FCSTD DOCUMENT  (FreeCAD 0.16R)
Label: PumpHolder
License: All rights reserved
LicenseURL: http://en.wikipedia.org/wiki/All_rights_reserved
objects: Sketcher::SketchObject×9, PartDesign::Pocket×5, PartDesign::Pad×3, PartDesign::Fillet×2, PartDesign::Chamfer×1, Mesh::Feature×1
note: 28 computed .brp shape members not serialized (recipe doc carries the construction recipe); baked Part::Feature solids carry a one-line shape summary decoded from their .brp

FEATURE [Sketcher::SketchObject] Sketch
  sketch-geometry (4):
    g0: LineSegment StartX=-10 StartY=52.5 StartZ=0 EndX=10 EndY=52.5 EndZ=0
    g1: LineSegment StartX=10 StartY=52.5 StartZ=0 EndX=10 EndY=-52.5 EndZ=0
    g2: LineSegment StartX=10 StartY=-52.5 StartZ=0 EndX=-10 EndY=-52.5 EndZ=0
    g3: LineSegment StartX=-10 StartY=-52.5 StartZ=0 EndX=-10 EndY=52.5 EndZ=0
  constraints (11):
    c: Coincident(g0,g1)
    c: Coincident(g1,g2)
    c: Coincident(g2,g3)
    c: Coincident(g3,g0)
    c: Horizontal(g0)
    c: Horizontal(g2)
    c: Vertical(g1)
    c: Vertical(g3)
    c: Symmetric(g0,g2,g-1)
    c: Distance(g1) = 105
    c: Distance(g2) = 20
FEATURE [PartDesign::Pad] Pad
  Length = 5
  Length2 = 100
  Sketch = -> Sketch
  Type = 0
FEATURE [Sketcher::SketchObject] Sketch004
  Placement = pos=(0,0,5) rot=(0,0,1;0rad)
  sketch-geometry (4):
    g0: LineSegment StartX=-7 StartY=52.5 StartZ=0 EndX=7 EndY=52.5 EndZ=0
    g1: LineSegment StartX=7 StartY=52.5 StartZ=0 EndX=7 EndY=-52.5 EndZ=0
    g2: LineSegment StartX=7 StartY=-52.5 StartZ=0 EndX=-7 EndY=-52.5 EndZ=0
    g3: LineSegment StartX=-7 StartY=-52.5 StartZ=0 EndX=-7 EndY=52.5 EndZ=0
  constraints (11):
    c: Coincident(g0,g1)
    c: Coincident(g1,g2)
    c: Coincident(g2,g3)
    c: Coincident(g3,g0)
    c: Horizontal(g0)
    c: Horizontal(g2)
    c: Vertical(g1)
    c: Vertical(g3)
    c: Symmetric(g2,g0,g-1)
    c: Distance(g0) = 14
    c: Distance(g1) = 105
FEATURE [Sketcher::SketchObject] Sketch005
  ExternalGeometry = -> [Pad]
  Placement = pos=(0,52.5,0) rot=(0,0.707107,0.707107;3.14159rad)
  Support = -> Pad [Face1]
  sketch-geometry (1):
    g0: Circle CenterX=0 CenterY=16 CenterZ=0 NormalX=0 NormalY=0 NormalZ=1 Radius=14
  constraints (3):
    c: PointOnObject(g0,g-2)
    c: Radius(g0) = 14
    c: Distance(g0,g-3) = 11
FEATURE [PartDesign::Pad] Pad001
  Length = 12
  Length2 = 100
  Reversed = true
  Sketch = -> Sketch005
  Type = 0
FEATURE [Sketcher::SketchObject] Sketch006
  ExternalGeometry = -> [Pad001]
  Placement = pos=(0,-52.5,0) rot=(1,0,0;1.5708rad)
  Support = -> Pad001 [Face4]
  sketch-geometry (1):
    g0: Circle CenterX=0 CenterY=16 CenterZ=0 NormalX=0 NormalY=0 NormalZ=1 Radius=15.7
  constraints (3):
    c: Radius(g0) = 15.7
    c: Distance(g0,g-3) = 11
    c: PointOnObject(g0,g-2)
FEATURE [PartDesign::Pad] Pad002
  Length = 12
  Length2 = 100
  Reversed = true
  Sketch = -> Sketch006
  Type = 0
FEATURE [Sketcher::SketchObject] Sketch007
  ExternalGeometry = -> [Pad002]
  Placement = pos=(0,-52.5,0) rot=(1,0,0;1.5708rad)
  Support = -> Pad002 [Face16]
  sketch-geometry (1):
    g0: Circle CenterX=0 CenterY=16 CenterZ=0 NormalX=0 NormalY=0 NormalZ=1 Radius=12.7
  constraints (2):
    c: Coincident(g0,g-3)
    c: Radius(g0) = 12.7
FEATURE [PartDesign::Pocket] Pocket
  Length = 25
  Sketch = -> Sketch007
  Type = 0
FEATURE [Sketcher::SketchObject] Sketch008
  ExternalGeometry = -> [Pocket]
  Placement = pos=(0,52.5,0) rot=(0,0.707107,0.707107;3.14159rad)
  Support = -> Pocket [Face17]
  sketch-geometry (1):
    g0: Circle CenterX=0 CenterY=16 CenterZ=0 NormalX=0 NormalY=0 NormalZ=1 Radius=11
  constraints (3):
    c: PointOnObject(g0,g-2)
    c: Radius(g0) = 11
    c: Coincident(g0,g-3)
FEATURE [PartDesign::Pocket] Pocket001
  Length = 15
  Sketch = -> Sketch008
  Type = 0
FEATURE [Sketcher::SketchObject] Sketch010
  Placement = pos=(0,52.5,0) rot=(0,0.707107,0.707107;3.14159rad)
  Support = -> Pocket001 [Face17]
  sketch-geometry (4):
    g0: LineSegment StartX=-8 StartY=63 StartZ=0 EndX=8 EndY=63 EndZ=0
    g1: LineSegment StartX=8 StartY=63 StartZ=0 EndX=8 EndY=13 EndZ=0
    g2: LineSegment StartX=8 StartY=13 StartZ=0 EndX=-8 EndY=13 EndZ=0
    g3: LineSegment StartX=-8 StartY=13 StartZ=0 EndX=-8 EndY=63 EndZ=0
  constraints (12):
    c: Coincident(g0,g1)
    c: Coincident(g1,g2)
    c: Coincident(g2,g3)
    c: Coincident(g3,g0)
    c: Horizontal(g0)
    c: Horizontal(g2)
    c: Vertical(g1)
    c: Vertical(g3)
    c: Distance(g2) = 16
    c: Symmetric(g1,g2,g-2)
    c: Distance(g1) = 50
    c: DistanceY(g1) = 13
FEATURE [PartDesign::Pocket] Pocket002
  Length = 5
  Sketch = -> Sketch010
  Type = 1
FEATURE [Sketcher::SketchObject] Sketch011
  Placement = pos=(0,0,5) rot=(0,0,1;0rad)
  Support = -> Pocket002 [Face6]
  sketch-geometry (2):
    g0: Circle CenterX=0 CenterY=-32 CenterZ=0 NormalX=0 NormalY=0 NormalZ=1 Radius=3
    g1: Circle CenterX=0 CenterY=32 CenterZ=0 NormalX=0 NormalY=0 NormalZ=1 Radius=3
  constraints (6):
    c: Radius(g1) = 3
    c: Equal(g1,g0)
    c: PointOnObject(g0,g-2)
    c: PointOnObject(g1,g-2)
    c: Distance(g0,g1) = 64
    c: Symmetric(g1,g0,g-1)
FEATURE [PartDesign::Pocket] Pocket003
  Length = 5
  Sketch = -> Sketch011
  Type = 1
FEATURE [Sketcher::SketchObject] Sketch012
  ExternalGeometry = -> [Pocket003]
  Placement = pos=(0,0,5) rot=(0,0,1;0rad)
  Support = -> Pocket003 [Face8]
  sketch-geometry (2):
    g0: Circle CenterX=0 CenterY=-32.0353 CenterZ=0 NormalX=0 NormalY=0 NormalZ=1 Radius=5
    g1: Circle CenterX=0 CenterY=32 CenterZ=0 NormalX=0 NormalY=0 NormalZ=1 Radius=5
  constraints (4):
    c: Radius(g1) = 5
    c: Equal(g1,g0)
    c: Coincident(g1,g-3)
    c: PointOnObject(g0,g-2)
FEATURE [PartDesign::Pocket] Pocket004
  Length = 3
  Sketch = -> Sketch012
  Type = 0
FEATURE [PartDesign::Fillet] Fillet
  Base = -> Pocket004 [Edge44,Edge91,Edge61,Edge98]
  Radius = 1
FEATURE [PartDesign::Chamfer] Chamfer
  Base = -> Fillet [Edge39,Edge85,Edge80,Edge63]
  Size = 1
FEATURE [PartDesign::Fillet] Fillet001
  Base = -> Chamfer [Edge3,Edge26]
  Radius = 1.1
FEATURE [Mesh::Feature] Mesh  label="Fillet001 (Meshed)"
